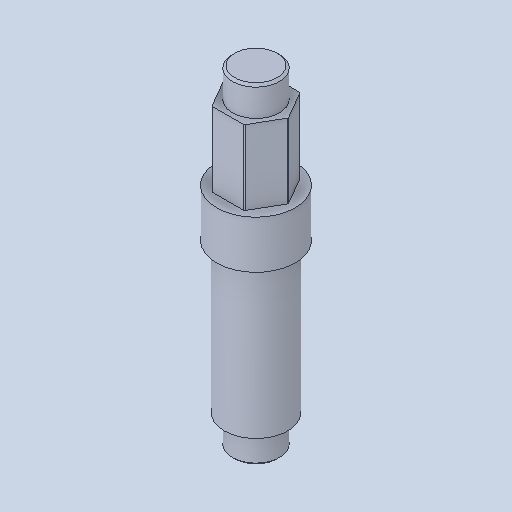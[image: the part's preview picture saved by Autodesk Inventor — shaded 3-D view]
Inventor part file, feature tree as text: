
AUTODESK INVENTOR PART (.ipt)
format: ipt  version: 2023 (Build 270158000, 158)  size: 113,664 bytes
history: native  units: in
note: dims shown in document units (in); Inventor stores cm internally (conversion verified against a paired STEP export)
features: chamfer x1
ambient origin geometry x8: Origin, YZ Plane, XZ Plane, XY Plane, X Axis, Y Axis, Z Axis, Center Point
bodies: Solid1 (feature_tree)
feature tree (1):
  chamfer  "Chamfer1"  [1 undecoded]
note: 1 required parameter value undecoded (feature->parameter linkage not recoverable at this tier; creation-order binding heuristic only, values carry confidence <= 0.55)
